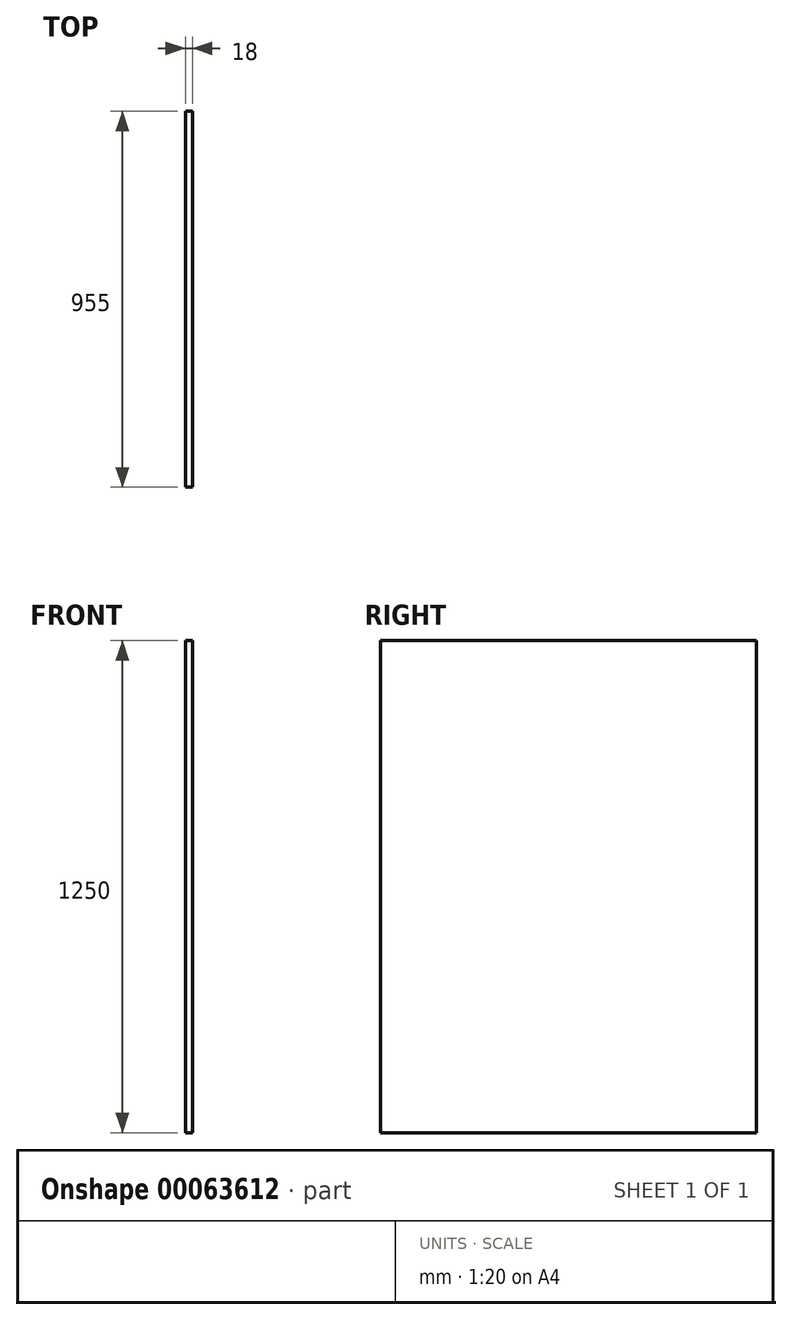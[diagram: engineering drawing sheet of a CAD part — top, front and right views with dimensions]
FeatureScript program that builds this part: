
annotation { "Feature Type Name" : "Feature", "Feature Type Description" : "" }
export const myFeature = defineFeature(function(context is Context, id is Id, definition is map)
    precondition{}
    {
        {
            var Q0;
            Q0=qCreatedBy(makeId("Right.planeOp"),FACE);
            var sketch = newSketch(context, id + "F0", { "sketchPlane" : qUnion([Q0])});
            skLineSegment(sketch, "E0.bottom", {"start": v(-474.52, 449.16) * mm, "end": v(480.48, 449.16) * mm});
            skLineSegment(sketch, "E0.top", {"start": v(-474.52, -800.84) * mm, "end": v(480.48, -800.84) * mm});
            skLineSegment(sketch, "E0.left", {"start": v(-474.52, 449.16) * mm, "end": v(-474.52, -800.84) * mm});
            skLineSegment(sketch, "E0.right", {"start": v(480.48, 449.16) * mm, "end": v(480.48, -800.84) * mm});
            skSolve(sketch);
        }
        {
            var Q0;
            Q0=makeQuery(id+"F0.imprint","IMPRINT",FACE,{"disambiguationData":[TD([[makeQuery(id+"F0.imprint","IMPRINT",EDGE,{"derivedFrom":sQuery(id+"F0.wireOp",EDGE,"E0.bottom")}),-1.0]])]});
            extrude(context, id + "F1", {"entities" : qUnion([Q0]), "depth" : 18 * mm});
        }
    });
